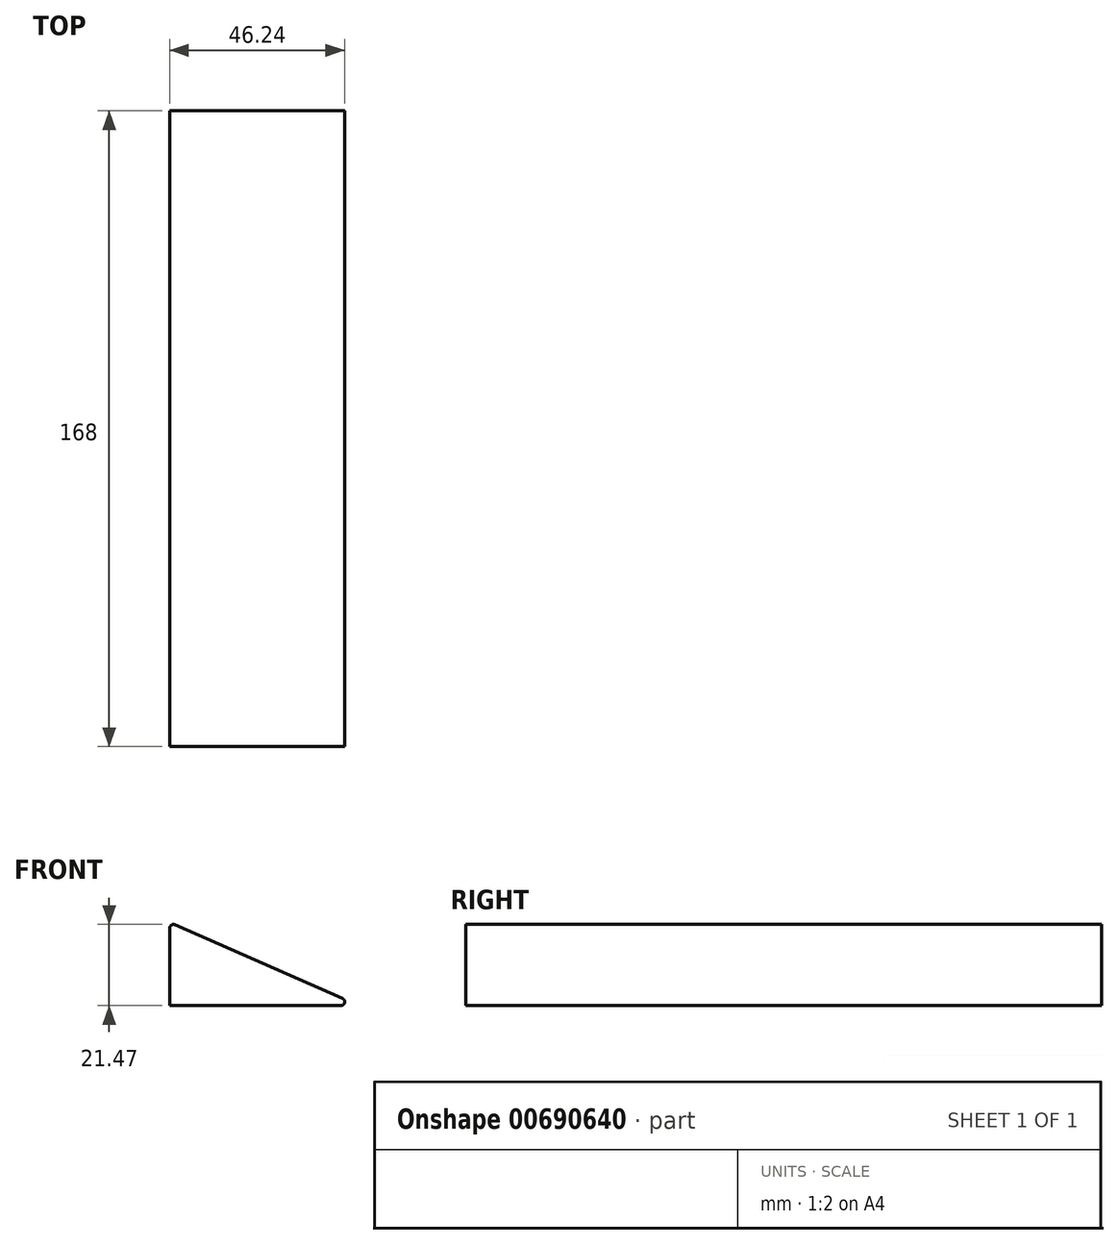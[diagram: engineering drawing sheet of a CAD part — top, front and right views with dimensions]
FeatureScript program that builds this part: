
annotation { "Feature Type Name" : "Feature", "Feature Type Description" : "" }
export const myFeature = defineFeature(function(context is Context, id is Id, definition is map)
    precondition{}
    {
        {
            var Q0;
            Q0=qCreatedBy(makeId("Front.planeOp"),FACE);
            var sketch = newSketch(context, id + "F0", { "sketchPlane" : qUnion([Q0])});
            skLineSegment(sketch, "E0", {"start": v(0, 0) * mm, "end": v(0, 22) * mm});
            skLineSegment(sketch, "E1", {"start": v(0, 22) * mm, "end": v(50, 0) * mm});
            skLineSegment(sketch, "E2", {"start": v(50, 0) * mm, "end": v(0, 0) * mm});
            skSolve(sketch);
        }
        {
            var Q0;
            Q0 = qSketchRegion(id + "F0", true);
            extrude(context, id + "F1", {"entities" : qUnion([Q0]), "depth" : 168 * mm, "offsetDistance" : 25.4 * mm});
        }
        {
            var Q0;
            Q0=makeQuery(id+"F1.opExtrude","SWEPT_EDGE",EDGE,{"disambiguationData":[OSD([sQuery(id+"F0.wireOp",EDGE,"E1"),sQuery(id+"F0.wireOp",EDGE,"E2")])]});
            var Q1;
            Q1=makeQuery(id+"F1.opExtrude","SWEPT_EDGE",EDGE,{"disambiguationData":[OSD([sQuery(id+"F0.wireOp",EDGE,"E0"),sQuery(id+"F0.wireOp",EDGE,"E1")])]});
            fillet(context, id + "F2", {"entities" : qUnion([Q0, Q1]), "radius" : 1 * mm, "tangentPropagation" : true, "allowEdgeOverflow" : false});
        }
    });
